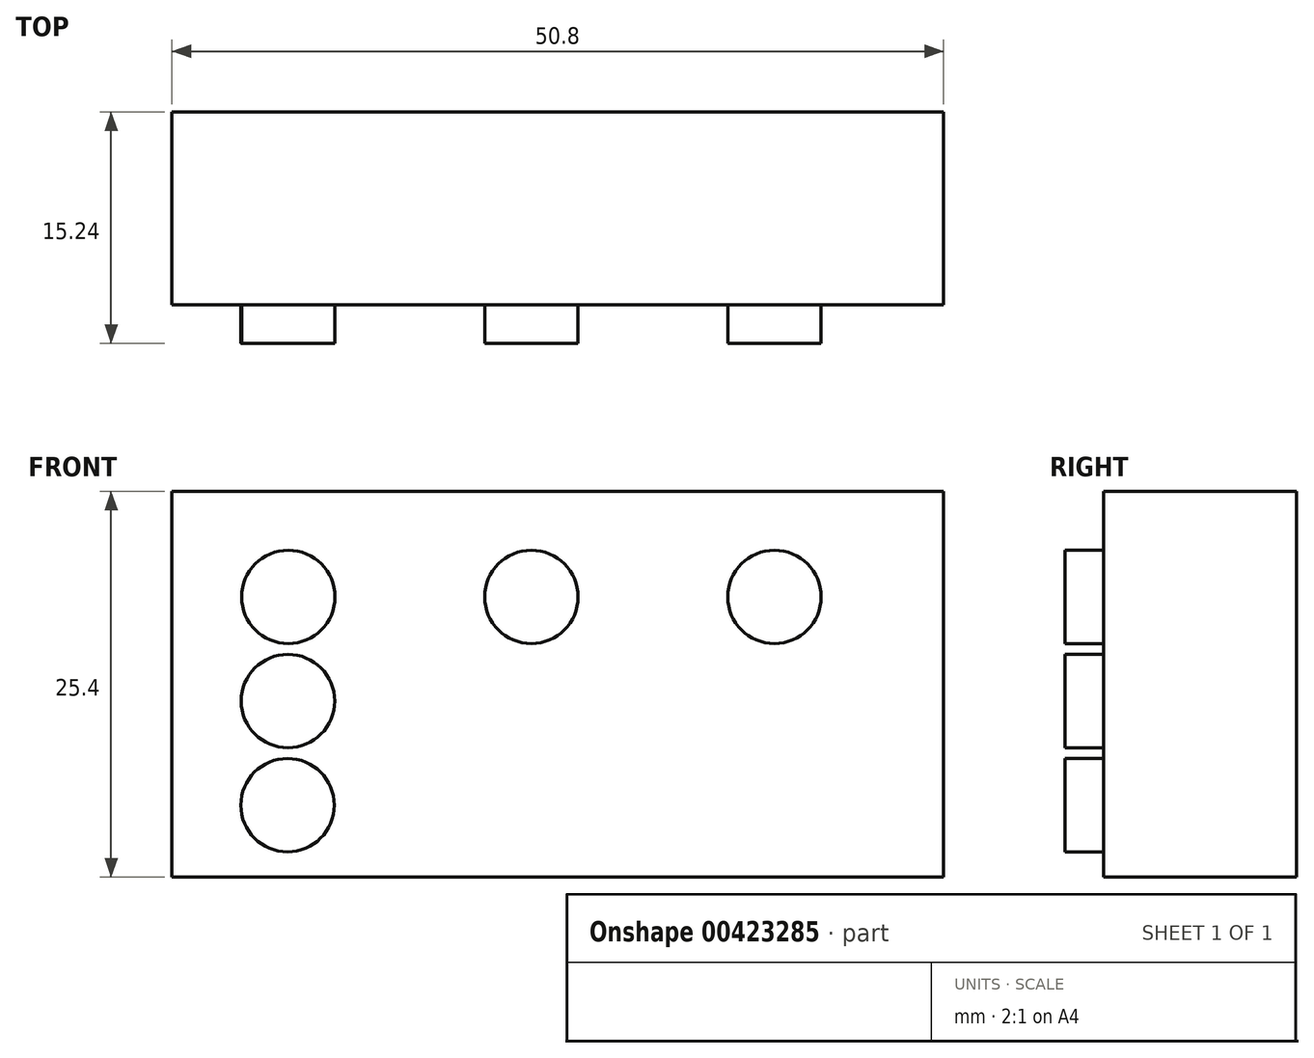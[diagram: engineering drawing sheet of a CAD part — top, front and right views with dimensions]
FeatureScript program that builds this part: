
annotation { "Feature Type Name" : "Feature", "Feature Type Description" : "" }
export const myFeature = defineFeature(function(context is Context, id is Id, definition is map)
    precondition{}
    {
        {
            var Q0;
            Q0=qCreatedBy(makeId("Front.planeOp"),FACE);
            var sketch = newSketch(context, id + "F0", { "sketchPlane" : qUnion([Q0])});
            skLineSegment(sketch, "E0.bottom", {"start": v(0, 0) * mm, "end": v(50.8, 0) * mm});
            skLineSegment(sketch, "E0.top", {"start": v(0, 25.4) * mm, "end": v(50.8, 25.4) * mm});
            skLineSegment(sketch, "E0.left", {"start": v(0, 0) * mm, "end": v(0, 25.4) * mm});
            skLineSegment(sketch, "E0.right", {"start": v(50.8, 0) * mm, "end": v(50.8, 25.4) * mm});
            skSolve(sketch);
        }
        {
            var Q0;
            Q0=makeQuery(id+"F0.imprint","IMPRINT",FACE,{"disambiguationData":[TD([[makeQuery(id+"F0.imprint","IMPRINT",EDGE,{"derivedFrom":sQuery(id+"F0.wireOp",EDGE,"E0.bottom")}),1.0]])]});
            extrude(context, id + "F1", {"entities" : qUnion([Q0]), "depth" : 12.7 * mm});
        }
        {
            var Q0;
            Q0=makeQuery(id+"F1.opExtrude","CAP_FACE",FACE,{"disambiguationData":[OSD([sQuery(id+"F0.wireOp",EDGE,"E0.bottom"),sQuery(id+"F0.wireOp",EDGE,"E0.top"),sQuery(id+"F0.wireOp",EDGE,"E0.left"),sQuery(id+"F0.wireOp",EDGE,"E0.right")])],"isStart":false});
            var sketch = newSketch(context, id + "F2", { "sketchPlane" : qUnion([Q0])});
            skCircle(sketch, "E1", {"center": v(7.66, 18.45) * mm, "radius": 3.08 * mm});
            skCircle(sketch, "E2.1.0.0", {"center": v(23.66, 18.45) * mm, "radius": 3.08 * mm});
            skCircle(sketch, "E2.2.0.0", {"center": v(39.67, 18.45) * mm, "radius": 3.08 * mm});
            skLineSegment(sketch, "E2.direction1", {"start": v(7.66, 18.45) * mm, "end": v(23.66, 18.45) * mm, "construction": true});
            skCircle(sketch, "E3.1.0.0", {"center": v(7.64, 11.6) * mm, "radius": 3.08 * mm});
            skCircle(sketch, "E3.2.0.0", {"center": v(7.61, 4.74) * mm, "radius": 3.08 * mm});
            skLineSegment(sketch, "E3.direction1", {"start": v(7.66, 18.45) * mm, "end": v(7.64, 11.6) * mm, "construction": true});
            skSolve(sketch);
        }
        {
            var Q0;
            Q0 = qSketchRegion(id + "F2", true);
            extrude(context, id + "F3", {"entities" : qUnion([Q0]), "operationType" : NewBodyOperationType.ADD, "depth" : 2.54 * mm});
        }
    });
